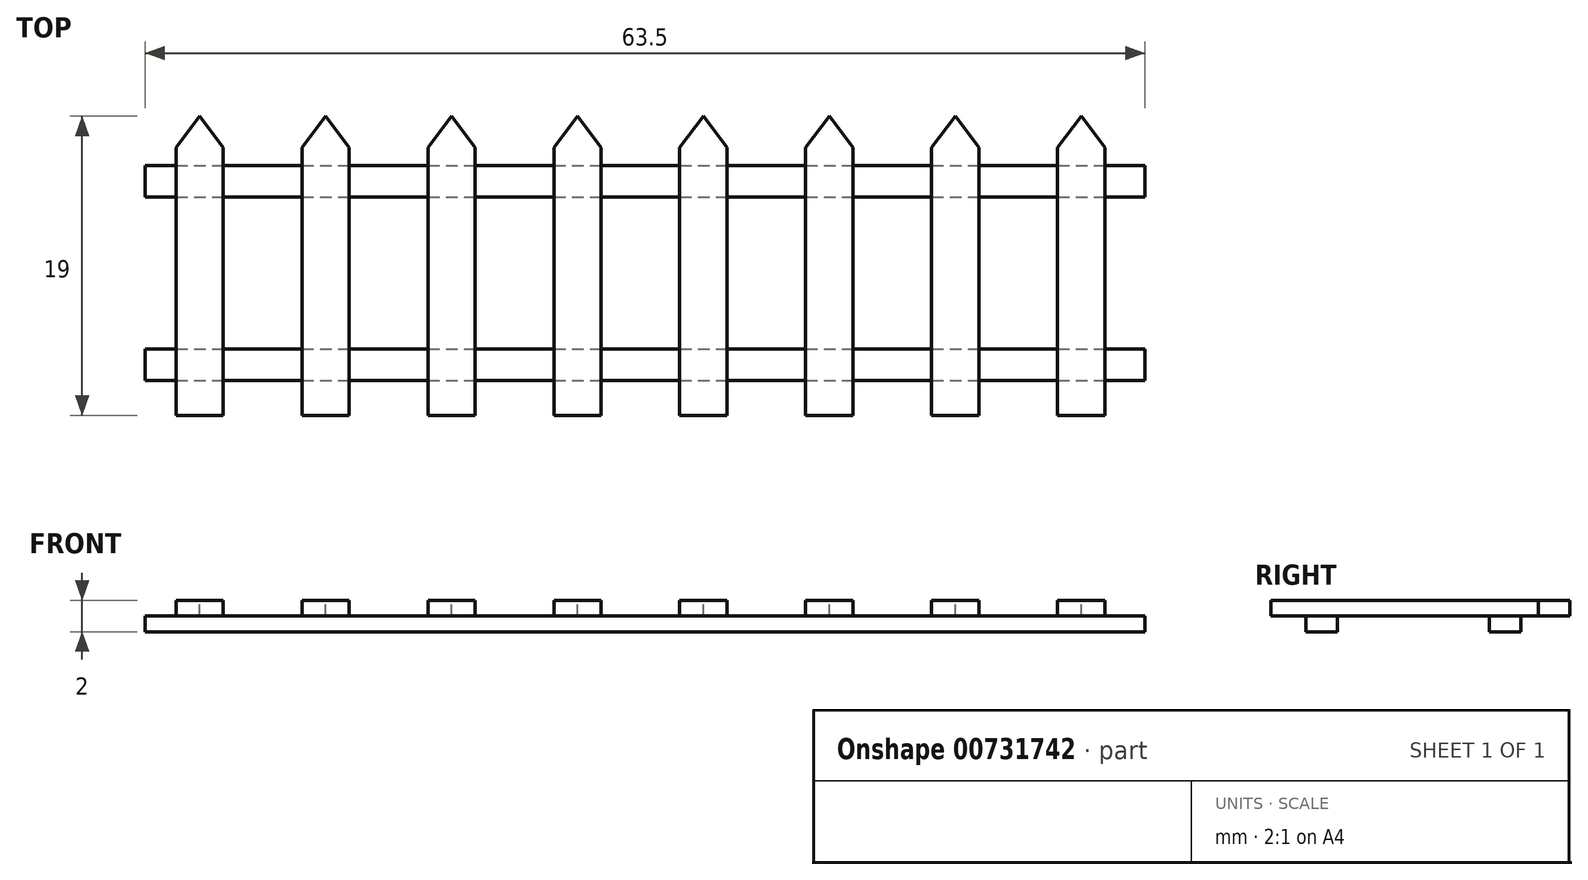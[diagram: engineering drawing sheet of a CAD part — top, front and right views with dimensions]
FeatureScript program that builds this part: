
annotation { "Feature Type Name" : "Feature", "Feature Type Description" : "" }
export const myFeature = defineFeature(function(context is Context, id is Id, definition is map)
    precondition{}
    {
        {
            var Q0;
            Q0=qCreatedBy(makeId("Top.planeOp"),FACE);
            var sketch = newSketch(context, id + "F0", { "sketchPlane" : qUnion([Q0])});
            skLineSegment(sketch, "E0.bottom", {"start": v(-64.04, 0) * mm, "end": v(-61.04, 0) * mm});
            skLineSegment(sketch, "E0.top", {"start": v(-64.04, 19) * mm, "end": v(-61.04, 19) * mm});
            skLineSegment(sketch, "E0.left", {"start": v(-64.04, 0) * mm, "end": v(-64.04, 19) * mm});
            skLineSegment(sketch, "E0.right", {"start": v(-61.04, 0) * mm, "end": v(-61.04, 19) * mm});
            skLineSegment(sketch, "E1.1.0.0", {"start": v(-56.04, 0) * mm, "end": v(-56.04, 19) * mm});
            skLineSegment(sketch, "E1.1.0.1", {"start": v(-53.04, 0) * mm, "end": v(-53.04, 19) * mm});
            skLineSegment(sketch, "E1.1.0.2", {"start": v(-56.04, 19) * mm, "end": v(-53.04, 19) * mm});
            skLineSegment(sketch, "E1.1.0.3", {"start": v(-56.04, 0) * mm, "end": v(-53.04, 0) * mm});
            skLineSegment(sketch, "E1.2.0.0", {"start": v(-48.04, 0) * mm, "end": v(-48.04, 19) * mm});
            skLineSegment(sketch, "E1.2.0.1", {"start": v(-45.04, 0) * mm, "end": v(-45.04, 19) * mm});
            skLineSegment(sketch, "E1.2.0.2", {"start": v(-48.04, 19) * mm, "end": v(-45.04, 19) * mm});
            skLineSegment(sketch, "E1.2.0.3", {"start": v(-48.04, 0) * mm, "end": v(-45.04, 0) * mm});
            skLineSegment(sketch, "E1.3.0.0", {"start": v(-40.04, 0) * mm, "end": v(-40.04, 19) * mm});
            skLineSegment(sketch, "E1.3.0.1", {"start": v(-37.04, 0) * mm, "end": v(-37.04, 19) * mm});
            skLineSegment(sketch, "E1.3.0.2", {"start": v(-40.04, 19) * mm, "end": v(-37.04, 19) * mm});
            skLineSegment(sketch, "E1.3.0.3", {"start": v(-40.04, 0) * mm, "end": v(-37.04, 0) * mm});
            skLineSegment(sketch, "E1.4.0.0", {"start": v(-32.04, 0) * mm, "end": v(-32.04, 19) * mm});
            skLineSegment(sketch, "E1.4.0.1", {"start": v(-29.04, 0) * mm, "end": v(-29.04, 19) * mm});
            skLineSegment(sketch, "E1.4.0.2", {"start": v(-32.04, 19) * mm, "end": v(-29.04, 19) * mm});
            skLineSegment(sketch, "E1.4.0.3", {"start": v(-32.04, 0) * mm, "end": v(-29.04, 0) * mm});
            skLineSegment(sketch, "E1.5.0.0", {"start": v(-24.04, 0) * mm, "end": v(-24.04, 19) * mm});
            skLineSegment(sketch, "E1.5.0.1", {"start": v(-21.04, 0) * mm, "end": v(-21.04, 19) * mm});
            skLineSegment(sketch, "E1.5.0.2", {"start": v(-24.04, 19) * mm, "end": v(-21.04, 19) * mm});
            skLineSegment(sketch, "E1.5.0.3", {"start": v(-24.04, 0) * mm, "end": v(-21.04, 0) * mm});
            skLineSegment(sketch, "E1.6.0.0", {"start": v(-16.04, 0) * mm, "end": v(-16.04, 19) * mm});
            skLineSegment(sketch, "E1.6.0.1", {"start": v(-13.04, 0) * mm, "end": v(-13.04, 19) * mm});
            skLineSegment(sketch, "E1.6.0.2", {"start": v(-16.04, 19) * mm, "end": v(-13.04, 19) * mm});
            skLineSegment(sketch, "E1.6.0.3", {"start": v(-16.04, 0) * mm, "end": v(-13.04, 0) * mm});
            skLineSegment(sketch, "E1.7.0.0", {"start": v(-8.04, 0) * mm, "end": v(-8.04, 19) * mm});
            skLineSegment(sketch, "E1.7.0.1", {"start": v(-5.04, 0) * mm, "end": v(-5.04, 19) * mm});
            skLineSegment(sketch, "E1.7.0.2", {"start": v(-8.04, 19) * mm, "end": v(-5.04, 19) * mm});
            skLineSegment(sketch, "E1.7.0.3", {"start": v(-8.04, 0) * mm, "end": v(-5.04, 0) * mm});
            skLineSegment(sketch, "E1.direction1", {"start": v(-64.04, 0) * mm, "end": v(-56.04, 0) * mm, "construction": true});
            skSolve(sketch);
        }
        {
            var Q0;
            Q0 = qSketchRegion(id + "F0", true);
            extrude(context, id + "F1", {"entities" : qUnion([Q0]), "depth" : 2 * mm, "offsetDistance" : 25 * mm, "hasSecondDirection" : true, "secondDirectionOppositeDirection" : true, "secondDirectionDepth" : -1 * mm});
        }
        {
            var Q0;
            Q0=qCreatedBy(makeId("Top.planeOp"),FACE);
            var sketch = newSketch(context, id + "F2", { "sketchPlane" : qUnion([Q0])});
            skLineSegment(sketch, "E2.bottom", {"start": v(-66, 15.86) * mm, "end": v(-2.5, 15.86) * mm});
            skLineSegment(sketch, "E2.top", {"start": v(-66, 13.86) * mm, "end": v(-2.5, 13.86) * mm});
            skLineSegment(sketch, "E2.left", {"start": v(-66, 15.86) * mm, "end": v(-66, 13.86) * mm});
            skLineSegment(sketch, "E2.right", {"start": v(-2.5, 15.86) * mm, "end": v(-2.5, 13.86) * mm});
            skLineSegment(sketch, "E3.bottom", {"start": v(-66, 4.22) * mm, "end": v(-2.5, 4.22) * mm});
            skLineSegment(sketch, "E3.top", {"start": v(-66, 2.22) * mm, "end": v(-2.5, 2.22) * mm});
            skLineSegment(sketch, "E3.left", {"start": v(-66, 4.22) * mm, "end": v(-66, 2.22) * mm});
            skLineSegment(sketch, "E3.right", {"start": v(-2.5, 4.22) * mm, "end": v(-2.5, 2.22) * mm});
            skSolve(sketch);
        }
        {
            var Q0;
            Q0 = qSketchRegion(id + "F2", true);
            extrude(context, id + "F3", {"entities" : qUnion([Q0]), "depth" : 1 * mm, "offsetDistance" : 25 * mm});
        }
        {
            var Q0;
            Q0=makeQuery(id+"F1.opExtrude","SWEPT_EDGE",EDGE,{"disambiguationData":[OSD([sQuery(id+"F0.wireOp",EDGE,"E0.top"),sQuery(id+"F0.wireOp",EDGE,"E0.left")])]});
            var Q1;
            Q1=makeQuery(id+"F1.opExtrude","SWEPT_EDGE",EDGE,{"disambiguationData":[OSD([sQuery(id+"F0.wireOp",EDGE,"E0.top"),sQuery(id+"F0.wireOp",EDGE,"E0.right")])]});
            var Q2;
            Q2=makeQuery(id+"F1.opExtrude","SWEPT_EDGE",EDGE,{"disambiguationData":[OSD([sQuery(id+"F0.wireOp",EDGE,"E1.1.0.0"),sQuery(id+"F0.wireOp",EDGE,"E1.1.0.2")])]});
            var Q3;
            Q3=makeQuery(id+"F1.opExtrude","SWEPT_EDGE",EDGE,{"disambiguationData":[OSD([sQuery(id+"F0.wireOp",EDGE,"E1.1.0.1"),sQuery(id+"F0.wireOp",EDGE,"E1.1.0.2")])]});
            var Q4;
            Q4=makeQuery(id+"F1.opExtrude","SWEPT_EDGE",EDGE,{"disambiguationData":[OSD([sQuery(id+"F0.wireOp",EDGE,"E1.2.0.0"),sQuery(id+"F0.wireOp",EDGE,"E1.2.0.2")])]});
            var Q5;
            Q5=makeQuery(id+"F1.opExtrude","SWEPT_EDGE",EDGE,{"disambiguationData":[OSD([sQuery(id+"F0.wireOp",EDGE,"E1.2.0.1"),sQuery(id+"F0.wireOp",EDGE,"E1.2.0.2")])]});
            var Q6;
            Q6=makeQuery(id+"F1.opExtrude","SWEPT_EDGE",EDGE,{"disambiguationData":[OSD([sQuery(id+"F0.wireOp",EDGE,"E1.3.0.0"),sQuery(id+"F0.wireOp",EDGE,"E1.3.0.2")])]});
            var Q7;
            Q7=makeQuery(id+"F1.opExtrude","SWEPT_EDGE",EDGE,{"disambiguationData":[OSD([sQuery(id+"F0.wireOp",EDGE,"E1.3.0.1"),sQuery(id+"F0.wireOp",EDGE,"E1.3.0.2")])]});
            var Q8;
            Q8=makeQuery(id+"F1.opExtrude","SWEPT_EDGE",EDGE,{"disambiguationData":[OSD([sQuery(id+"F0.wireOp",EDGE,"E1.4.0.0"),sQuery(id+"F0.wireOp",EDGE,"E1.4.0.2")])]});
            var Q9;
            Q9=makeQuery(id+"F1.opExtrude","SWEPT_EDGE",EDGE,{"disambiguationData":[OSD([sQuery(id+"F0.wireOp",EDGE,"E1.4.0.1"),sQuery(id+"F0.wireOp",EDGE,"E1.4.0.2")])]});
            var Q10;
            Q10=makeQuery(id+"F1.opExtrude","SWEPT_EDGE",EDGE,{"disambiguationData":[OSD([sQuery(id+"F0.wireOp",EDGE,"E1.6.0.0"),sQuery(id+"F0.wireOp",EDGE,"E1.6.0.2")])]});
            var Q11;
            Q11=makeQuery(id+"F1.opExtrude","SWEPT_EDGE",EDGE,{"disambiguationData":[OSD([sQuery(id+"F0.wireOp",EDGE,"E1.6.0.1"),sQuery(id+"F0.wireOp",EDGE,"E1.6.0.2")])]});
            var Q12;
            Q12=makeQuery(id+"F1.opExtrude","SWEPT_EDGE",EDGE,{"disambiguationData":[OSD([sQuery(id+"F0.wireOp",EDGE,"E1.7.0.0"),sQuery(id+"F0.wireOp",EDGE,"E1.7.0.2")])]});
            var Q13;
            Q13=makeQuery(id+"F1.opExtrude","SWEPT_EDGE",EDGE,{"disambiguationData":[OSD([sQuery(id+"F0.wireOp",EDGE,"E1.7.0.1"),sQuery(id+"F0.wireOp",EDGE,"E1.7.0.2")])]});
            var Q14;
            Q14=makeQuery(id+"F1.opExtrude","SWEPT_EDGE",EDGE,{"disambiguationData":[OSD([sQuery(id+"F0.wireOp",EDGE,"E1.5.0.0"),sQuery(id+"F0.wireOp",EDGE,"E1.5.0.2")])]});
            var Q15;
            Q15=makeQuery(id+"F1.opExtrude","SWEPT_EDGE",EDGE,{"disambiguationData":[OSD([sQuery(id+"F0.wireOp",EDGE,"E1.5.0.1"),sQuery(id+"F0.wireOp",EDGE,"E1.5.0.2")])]});
            chamfer(context, id + "F4", {"entities" : qUnion([Q0, Q1, Q2, Q3, Q4, Q5, Q6, Q7, Q8, Q9, Q10, Q11, Q12, Q13, Q14, Q15]), "chamferType" : ChamferType.TWO_OFFSETS, "width1" : 2 * mm, "oppositeDirection" : false, "width2" : 1.5 * mm, "tangentPropagation" : true});
        }
    });
